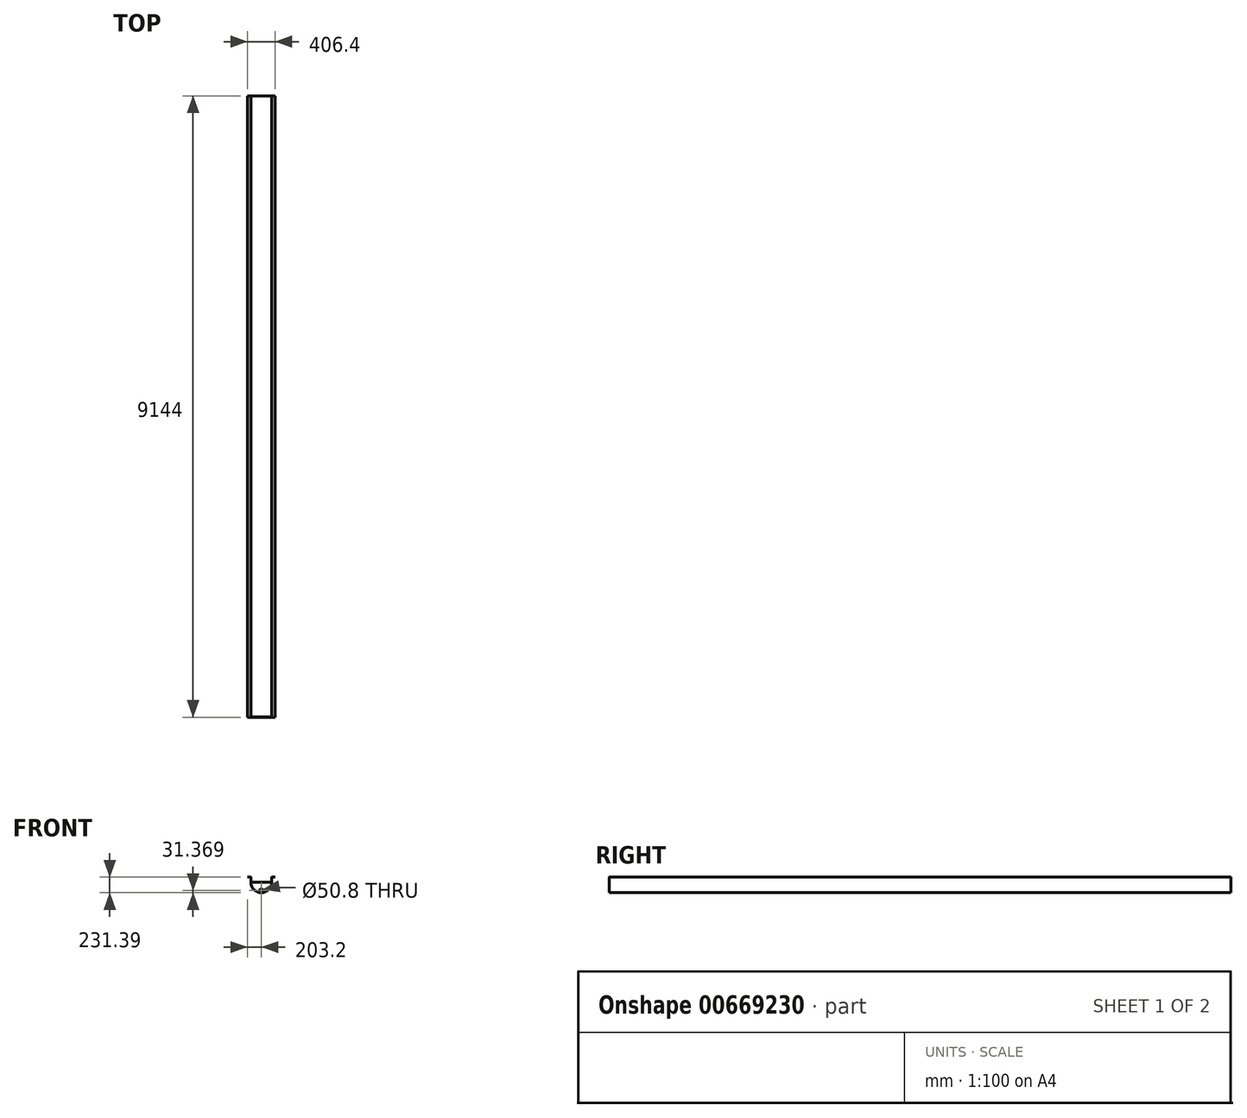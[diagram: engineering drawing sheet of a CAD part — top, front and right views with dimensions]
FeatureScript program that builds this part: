
annotation { "Feature Type Name" : "Feature", "Feature Type Description" : "" }
export const myFeature = defineFeature(function(context is Context, id is Id, definition is map)
    precondition{}
    {
        {
            var Q0;
            Q0=qCreatedBy(makeId("Front.planeOp"),FACE);
            var sketch = newSketch(context, id + "F0", { "sketchPlane" : qUnion([Q0])});
            skLineSegment(sketch, "E0.left", {"start": v(152.4, 0) * mm, "end": v(152.4, 72.4) * mm});
            skLineSegment(sketch, "E0.right", {"start": v(-152.4, 0) * mm, "end": v(-152.4, 76.2) * mm});
            skPoint(sketch, "E0.middle", {"position": v(0, 38.1) * mm});
            skArc(sketch, "E1", {"start": v(-152.4, 0) * mm, "mid": v(0, -152.4) * mm, "end": v(152.4, 0) * mm});
            skLineSegment(sketch, "E2.0", {"start": v(149.6, 0) * mm, "end": v(149.6, 72.4) * mm});
            skArc(sketch, "E2.1", {"start": v(-149.6, 0) * mm, "mid": v(0, -149.6) * mm, "end": v(149.6, 0) * mm});
            skLineSegment(sketch, "E2.2", {"start": v(-149.6, 0) * mm, "end": v(-149.6, 72.4) * mm});
            skLineSegment(sketch, "E3", {"start": v(156.21, 76.2) * mm, "end": v(203.2, 76.2) * mm});
            skLineSegment(sketch, "E4", {"start": v(203.2, 79) * mm, "end": v(203.2, 76.2) * mm});
            skPoint(sketch, "E5.visualSharp", {"position": v(152.4, 76.2) * mm});
            skArc(sketch, "E5.filletArc", {"start": v(156.21, 76.2) * mm, "mid": v(153.52, 75.08) * mm, "end": v(152.4, 72.4) * mm});
            skPoint(sketch, "E6.visualSharp", {"position": v(149.6, 76.2) * mm});
            skArc(sketch, "E7.0", {"start": v(156.21, 79) * mm, "mid": v(151.54, 77.06) * mm, "end": v(149.6, 72.4) * mm});
            skLineSegment(sketch, "E7.1", {"start": v(156.21, 79) * mm, "end": v(203.2, 79) * mm});
            skLineSegment(sketch, "E8.MirrorCS", {"start": v(-203.2, 79) * mm, "end": v(-203.2, 76.2) * mm});
            skArc(sketch, "E9.MirrorCS", {"start": v(-156.21, 76.2) * mm, "mid": v(-153.52, 75.08) * mm, "end": v(-152.4, 72.4) * mm});
            skPoint(sketch, "E10.MirrorP", {"position": v(-149.6, 76.2) * mm});
            skArc(sketch, "E11.MirrorCS", {"start": v(-156.21, 79) * mm, "mid": v(-151.54, 77.06) * mm, "end": v(-149.6, 72.4) * mm});
            skPoint(sketch, "E12.MirrorP", {"position": v(-152.4, 76.2) * mm});
            skLineSegment(sketch, "E13.MirrorCS", {"start": v(-156.21, 76.2) * mm, "end": v(-203.2, 76.2) * mm});
            skLineSegment(sketch, "E14.MirrorCS", {"start": v(-156.21, 79) * mm, "end": v(-203.2, 79) * mm});
            skSolve(sketch);
        }
        {
            var Q0;
            Q0 = qSketchRegion(id + "F0", true);
            extrude(context, id + "F1", {"entities" : qUnion([Q0]), "endBound" : BoundingType.SYMMETRIC, "depth" : 9144 * mm, "offsetDistance" : 25.4 * mm});
        }
        {
            var Q0;
            Q0=makeQuery(id+"F1.opExtrude","CAP_FACE",FACE,{"disambiguationData":[OSD([sQuery(id+"F0.wireOp",EDGE,"E0.left"),sQuery(id+"F0.wireOp",EDGE,"E0.right"),sQuery(id+"F0.wireOp",EDGE,"E1"),sQuery(id+"F0.wireOp",EDGE,"E2.0"),sQuery(id+"F0.wireOp",EDGE,"E2.1"),sQuery(id+"F0.wireOp",EDGE,"E2.2"),sQuery(id+"F0.wireOp",EDGE,"E3"),sQuery(id+"F0.wireOp",EDGE,"E4"),sQuery(id+"F0.wireOp",EDGE,"E5.filletArc"),sQuery(id+"F0.wireOp",EDGE,"E7.0"),sQuery(id+"F0.wireOp",EDGE,"E7.1"),sQuery(id+"F0.wireOp",EDGE,"E8.MirrorCS"),sQuery(id+"F0.wireOp",EDGE,"E9.MirrorCS"),sQuery(id+"F0.wireOp",EDGE,"E11.MirrorCS"),sQuery(id+"F0.wireOp",EDGE,"E13.MirrorCS"),sQuery(id+"F0.wireOp",EDGE,"E14.MirrorCS")])],"isStart":false});
            var sketch = newSketch(context, id + "F2", { "sketchPlane" : qUnion([Q0])});
            skLineSegment(sketch, "E15", {"start": v(-152.4, 0) * mm, "end": v(152.4, 0) * mm});
            skArc(sketch, "E16.0", {"start": v(-152.4, 0) * mm, "mid": v(0, -152.4) * mm, "end": v(152.4, 0) * mm});
            skPoint(sketch, "E17", {"position": v(0, -121.03) * mm});
            skSolve(sketch);
        }
        {
            var Q0;
            Q0 = qSketchRegion(id + "F2", true);
            extrude(context, id + "F3", {"entities" : qUnion([Q0]), "operationType" : NewBodyOperationType.ADD, "oppositeDirection" : true, "depth" : 3.17 * mm, "offsetDistance" : 25.4 * mm});
        }
        {
            var Q0;
            Q0=makeQuery(id+"F1.opExtrude","CAP_FACE",FACE,{"disambiguationData":[OSD([sQuery(id+"F0.wireOp",EDGE,"E0.left"),sQuery(id+"F0.wireOp",EDGE,"E0.right"),sQuery(id+"F0.wireOp",EDGE,"E1"),sQuery(id+"F0.wireOp",EDGE,"E2.0"),sQuery(id+"F0.wireOp",EDGE,"E2.1"),sQuery(id+"F0.wireOp",EDGE,"E2.2"),sQuery(id+"F0.wireOp",EDGE,"E3"),sQuery(id+"F0.wireOp",EDGE,"E4"),sQuery(id+"F0.wireOp",EDGE,"E5.filletArc"),sQuery(id+"F0.wireOp",EDGE,"E7.0"),sQuery(id+"F0.wireOp",EDGE,"E7.1"),sQuery(id+"F0.wireOp",EDGE,"E8.MirrorCS"),sQuery(id+"F0.wireOp",EDGE,"E9.MirrorCS"),sQuery(id+"F0.wireOp",EDGE,"E11.MirrorCS"),sQuery(id+"F0.wireOp",EDGE,"E13.MirrorCS"),sQuery(id+"F0.wireOp",EDGE,"E14.MirrorCS")])],"isStart":true});
            var sketch = newSketch(context, id + "F4", { "sketchPlane" : qUnion([Q0])});
            skArc(sketch, "E18.0", {"start": v(149.6, 0) * mm, "mid": v(0, -149.6) * mm, "end": v(-149.6, 0) * mm});
            skLineSegment(sketch, "E19.0", {"start": v(149.6, 0) * mm, "end": v(-149.6, 0) * mm});
            skSolve(sketch);
        }
        {
            var Q0;
            Q0 = qSketchRegion(id + "F4", true);
            extrude(context, id + "F5", {"entities" : qUnion([Q0]), "operationType" : NewBodyOperationType.ADD, "oppositeDirection" : true, "depth" : 2.8 * mm, "offsetDistance" : 25.4 * mm});
        }
        {
            var Q0;
            Q0=sQuery(id+"F2.wireOp",VERTEX,"E17");
            var Q1;
            Q1=makeQuery(id+"F1.opExtrude","SWEPT_BODY",BODY,{"disambiguationData":[OSD([sQuery(id+"F0.wireOp",EDGE,"E0.left"),sQuery(id+"F0.wireOp",EDGE,"E0.right"),sQuery(id+"F0.wireOp",EDGE,"E1"),sQuery(id+"F0.wireOp",EDGE,"E2.0"),sQuery(id+"F0.wireOp",EDGE,"E2.1"),sQuery(id+"F0.wireOp",EDGE,"E2.2"),sQuery(id+"F0.wireOp",EDGE,"E3"),sQuery(id+"F0.wireOp",EDGE,"E4"),sQuery(id+"F0.wireOp",EDGE,"E5.filletArc"),sQuery(id+"F0.wireOp",EDGE,"E7.0"),sQuery(id+"F0.wireOp",EDGE,"E7.1"),sQuery(id+"F0.wireOp",EDGE,"E8.MirrorCS"),sQuery(id+"F0.wireOp",EDGE,"E9.MirrorCS"),sQuery(id+"F0.wireOp",EDGE,"E11.MirrorCS"),sQuery(id+"F0.wireOp",EDGE,"E13.MirrorCS"),sQuery(id+"F0.wireOp",EDGE,"E14.MirrorCS")])]});
            hole(context, id + "F6", {"style" : HoleStyle.SIMPLE, "endStyle" : HoleEndStyle.BLIND, "holeDiameter" : 50.8 * mm, "majorDiameter" : 6.35 * mm, "holeDepth" : 12.7 * mm, "isTappedThrough" : true, "tappedDepth" : 12.7 * mm, "tapClearance" : 3, "locations" : qUnion([Q0]), "scope" : qUnion([Q1])});
        }
    });
